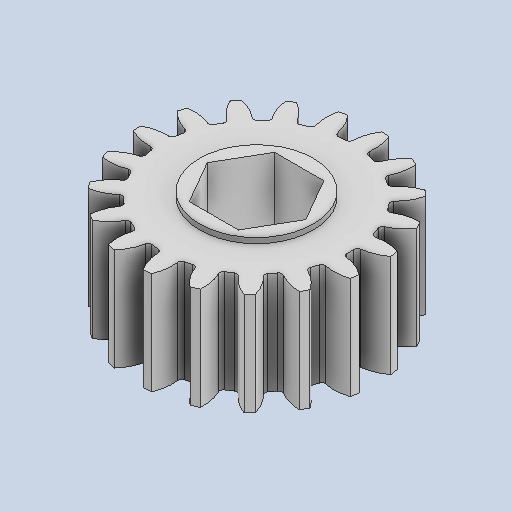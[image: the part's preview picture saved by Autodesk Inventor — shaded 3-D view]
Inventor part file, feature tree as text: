
AUTODESK INVENTOR PART (.ipt)
format: ipt  version: 2022.3 (Build 263350000, 350)  size: 256,512 bytes
history: native  units: in
note: dims shown in document units (in); Inventor stores cm internally (conversion verified against a paired STEP export)
features: fillet x1
ambient origin geometry x8: Origin, YZ Plane, XZ Plane, XY Plane, X Axis, Y Axis, Z Axis, Center Point
bodies: Solid1 (feature_tree)
feature tree (1):
  fillet  "Fillet1"  [1 undecoded]
note: 1 required parameter value undecoded (feature->parameter linkage not recoverable at this tier; creation-order binding heuristic only, values carry confidence <= 0.55)
